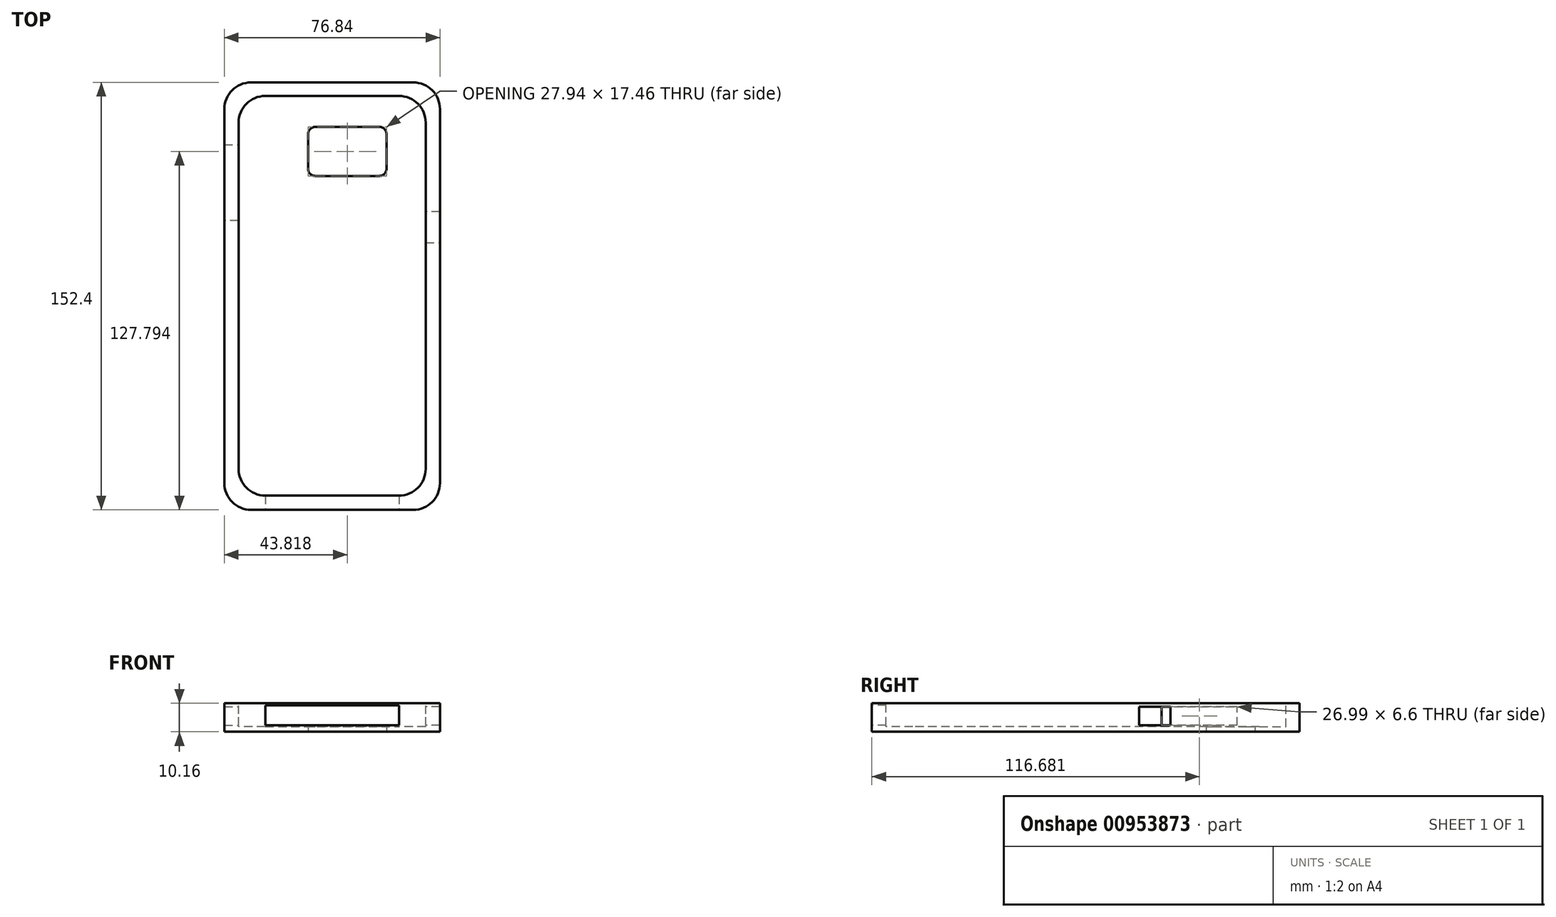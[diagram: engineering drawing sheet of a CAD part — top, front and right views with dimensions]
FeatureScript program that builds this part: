
annotation { "Feature Type Name" : "Feature", "Feature Type Description" : "" }
export const myFeature = defineFeature(function(context is Context, id is Id, definition is map)
    precondition{}
    {
        {
            var Q0;
            Q0=qCreatedBy(makeId("Top.planeOp"),FACE);
            var sketch = newSketch(context, id + "F0", { "sketchPlane" : qUnion([Q0])});
            skLineSegment(sketch, "E0.bottom", {"start": v(33.34, -71.12) * mm, "end": v(-33.34, -71.12) * mm});
            skLineSegment(sketch, "E0.top", {"start": v(33.34, 71.12) * mm, "end": v(-33.34, 71.12) * mm});
            skLineSegment(sketch, "E0.left", {"start": v(33.34, -71.12) * mm, "end": v(33.34, 71.12) * mm});
            skLineSegment(sketch, "E0.right", {"start": v(-33.34, -71.12) * mm, "end": v(-33.34, 71.12) * mm});
            skPoint(sketch, "E0.middle", {"position": v(0, 0) * mm});
            skPoint(sketch, "E1.endSnap0", {"position": v(0, -76.2) * mm});
            skLineSegment(sketch, "E2", {"start": v(38.42, -76.2) * mm, "end": v(38.42, 76.2) * mm});
            skLineSegment(sketch, "E3", {"start": v(38.42, 76.2) * mm, "end": v(-38.42, 76.2) * mm});
            skLineSegment(sketch, "E4", {"start": v(-38.42, 76.2) * mm, "end": v(-38.42, -76.2) * mm});
            skLineSegment(sketch, "E5", {"start": v(38.42, -76.2) * mm, "end": v(-38.42, -76.2) * mm});
            skLineSegment(sketch, "E6", {"start": v(-33.34, -71.12) * mm, "end": v(-33.34, -76.2) * mm});
            skSolve(sketch);
        }
        {
            var Q0;
            Q0=makeQuery(id+"F0.imprint","IMPRINT",FACE,{"disambiguationData":[TD([[makeQuery(id+"F0.imprint","IMPRINT",EDGE,{"derivedFrom":sQuery(id+"F0.wireOp",EDGE,"E0.bottom")}),1.0]])]});
            var Q1;
            Q1=makeQuery(id+"F0.imprint","IMPRINT",FACE,{"disambiguationData":[TD([[makeQuery(id+"F0.imprint","IMPRINT",EDGE,{"derivedFrom":sQuery(id+"F0.wireOp",EDGE,"E0.bottom")}),-1.0]])]});
            extrude(context, id + "F1", {"entities" : qUnion([Q0, Q1]), "depth" : 10.16 * mm, "offsetDistance" : 25.4 * mm});
        }
        {
            var Q0;
            Q0=makeQuery(id+"F1.opExtrude","CAP_FACE",FACE,{"disambiguationData":[OSD([sQuery(id+"F0.wireOp",EDGE,"E2"),sQuery(id+"F0.wireOp",EDGE,"E3"),sQuery(id+"F0.wireOp",EDGE,"E4"),sQuery(id+"F0.wireOp",EDGE,"E5")])],"isStart":false});
            var sketch = newSketch(context, id + "F2", { "sketchPlane" : qUnion([Q0])});
            skLineSegment(sketch, "E7", {"start": v(-38.42, -76.2) * mm, "end": v(-33.34, -76.2) * mm});
            skLineSegment(sketch, "E8", {"start": v(-33.34, -76.2) * mm, "end": v(-33.34, -71.12) * mm});
            skLineSegment(sketch, "E9", {"start": v(-33.34, -71.12) * mm, "end": v(33.34, -71.12) * mm});
            skLineSegment(sketch, "E10", {"start": v(33.34, -71.12) * mm, "end": v(33.34, 71.37) * mm});
            skLineSegment(sketch, "E11", {"start": v(33.34, 71.37) * mm, "end": v(-33.34, 71.37) * mm});
            skLineSegment(sketch, "E12", {"start": v(-33.34, 71.37) * mm, "end": v(-33.34, -71.12) * mm});
            skSolve(sketch);
        }
        {
            var Q0;
            Q0=makeQuery(id+"F2.imprint","IMPRINT",FACE,{"disambiguationData":[TD([[makeQuery(id+"F2.imprint","IMPRINT",EDGE,{"derivedFrom":sQuery(id+"F2.wireOp",EDGE,"E9")}),1.0]])]});
            extrude(context, id + "F3", {"entities" : qUnion([Q0]), "operationType" : NewBodyOperationType.REMOVE, "oppositeDirection" : true, "depth" : 8.38 * mm, "offsetDistance" : 25.4 * mm});
        }
        {
            var Q0;
            Q0=makeQuery(id+"F1.opExtrude","SWEPT_EDGE",EDGE,{"disambiguationData":[OSD([sQuery(id+"F0.wireOp",EDGE,"E3"),sQuery(id+"F0.wireOp",EDGE,"E4")])]});
            var Q1;
            Q1=makeQuery(id+"F1.opExtrude","SWEPT_EDGE",EDGE,{"disambiguationData":[OSD([sQuery(id+"F0.wireOp",EDGE,"E4"),sQuery(id+"F0.wireOp",EDGE,"E5")])]});
            var Q2;
            Q2=makeQuery(id+"F3.boolean.opBoolean","COPY",EDGE,{"derivedFrom":makeQuery(id+"F3.opExtrude","SWEPT_EDGE",EDGE,{"disambiguationData":[OSD([sQuery(id+"F2.wireOp",EDGE,"E11"),sQuery(id+"F2.wireOp",EDGE,"E12")])]})});
            var Q3;
            Q3=makeQuery(id+"F3.boolean.opBoolean","COPY",EDGE,{"derivedFrom":makeQuery(id+"F3.opExtrude","SWEPT_EDGE",EDGE,{"disambiguationData":[OSD([sQuery(id+"F2.wireOp",EDGE,"E9"),sQuery(id+"F2.wireOp",EDGE,"E12")])]})});
            var Q4;
            Q4=makeQuery(id+"F3.boolean.opBoolean","COPY",EDGE,{"derivedFrom":makeQuery(id+"F3.opExtrude","SWEPT_EDGE",EDGE,{"disambiguationData":[OSD([sQuery(id+"F2.wireOp",EDGE,"E9"),sQuery(id+"F2.wireOp",EDGE,"E10")])]})});
            var Q5;
            Q5=makeQuery(id+"F1.opExtrude","SWEPT_EDGE",EDGE,{"disambiguationData":[OSD([sQuery(id+"F0.wireOp",EDGE,"E2"),sQuery(id+"F0.wireOp",EDGE,"E5")])]});
            var Q6;
            Q6=makeQuery(id+"F1.opExtrude","SWEPT_EDGE",EDGE,{"disambiguationData":[OSD([sQuery(id+"F0.wireOp",EDGE,"E2"),sQuery(id+"F0.wireOp",EDGE,"E3")])]});
            var Q7;
            Q7=makeQuery(id+"F3.boolean.opBoolean","COPY",EDGE,{"derivedFrom":makeQuery(id+"F3.opExtrude","SWEPT_EDGE",EDGE,{"disambiguationData":[OSD([sQuery(id+"F2.wireOp",EDGE,"E10"),sQuery(id+"F2.wireOp",EDGE,"E11")])]})});
            fillet(context, id + "F4", {"entities" : qUnion([Q0, Q1, Q2, Q3, Q4, Q5, Q6, Q7]), "radius" : 9.52 * mm, "tangentPropagation" : true, "allowEdgeOverflow" : false});
        }
        {
            var Q0;
            Q0=makeQuery(id+"F1.opExtrude","CAP_FACE",FACE,{"disambiguationData":[OSD([sQuery(id+"F0.wireOp",EDGE,"E2"),sQuery(id+"F0.wireOp",EDGE,"E3"),sQuery(id+"F0.wireOp",EDGE,"E4"),sQuery(id+"F0.wireOp",EDGE,"E5")])],"isStart":false});
            var sketch = newSketch(context, id + "F5", { "sketchPlane" : qUnion([Q0])});
            skLineSegment(sketch, "E13", {"start": v(-38.42, 76.2) * mm, "end": v(-28.9, 76.2) * mm});
            skLineSegment(sketch, "E14", {"start": v(-38.42, 76.2) * mm, "end": v(-38.42, 53.98) * mm});
            skLineSegment(sketch, "E15", {"start": v(-38.42, 53.98) * mm, "end": v(-38.42, 26.99) * mm});
            skLineSegment(sketch, "E16", {"start": v(-28.9, 76.2) * mm, "end": v(38.42, 76.2) * mm});
            skLineSegment(sketch, "E17", {"start": v(38.42, 76.2) * mm, "end": v(38.42, 30.16) * mm});
            skLineSegment(sketch, "E18", {"start": v(38.42, 30.16) * mm, "end": v(38.42, 19.05) * mm});
            skLineSegment(sketch, "E19", {"start": v(38.42, 30.16) * mm, "end": v(33.34, 30.16) * mm});
            skLineSegment(sketch, "E20", {"start": v(33.34, 19.05) * mm, "end": v(38.42, 19.05) * mm});
            skLineSegment(sketch, "E21", {"start": v(33.34, 30.16) * mm, "end": v(33.34, 19.05) * mm});
            skLineSegment(sketch, "E22", {"start": v(-38.42, 53.98) * mm, "end": v(-33.34, 53.98) * mm});
            skLineSegment(sketch, "E23", {"start": v(-33.34, 53.98) * mm, "end": v(-33.34, 26.99) * mm});
            skLineSegment(sketch, "E24", {"start": v(-33.34, 26.99) * mm, "end": v(-38.42, 26.99) * mm});
            skLineSegment(sketch, "E25", {"start": v(23.81, -71.12) * mm, "end": v(-23.81, -71.12) * mm});
            skLineSegment(sketch, "E26", {"start": v(-23.81, -71.12) * mm, "end": v(-23.81, -76.2) * mm});
            skLineSegment(sketch, "E27", {"start": v(-23.81, -76.2) * mm, "end": v(23.81, -76.2) * mm});
            skLineSegment(sketch, "E28", {"start": v(23.81, -71.12) * mm, "end": v(23.81, -76.2) * mm});
            skSolve(sketch);
        }
        {
            var Q0;
            Q0=makeQuery(id+"F5.imprint","IMPRINT",FACE,{"disambiguationData":[TD([[makeQuery(id+"F5.imprint","IMPRINT",EDGE,{"derivedFrom":sQuery(id+"F5.wireOp",EDGE,"E25")}),-1.0]])]});
            var Q1;
            Q1=makeQuery(id+"F5.imprint","IMPRINT",FACE,{"disambiguationData":[TD([[makeQuery(id+"F5.imprint","IMPRINT",EDGE,{"derivedFrom":sQuery(id+"F5.wireOp",EDGE,"E18")}),1.0]])]});
            var Q2;
            Q2=makeQuery(id+"F5.imprint","IMPRINT",FACE,{"disambiguationData":[TD([[makeQuery(id+"F5.imprint","IMPRINT",EDGE,{"derivedFrom":sQuery(id+"F5.wireOp",EDGE,"E15")}),1.0]])]});
            extrude(context, id + "F6", {"entities" : qUnion([Q0, Q1, Q2]), "operationType" : NewBodyOperationType.REMOVE, "oppositeDirection" : true, "depth" : 7.87 * mm, "offsetDistance" : 25.4 * mm});
        }
        {
            var Q0;
            Q0=makeQuery(id+"F1.opExtrude","CAP_FACE",FACE,{"disambiguationData":[OSD([sQuery(id+"F0.wireOp",EDGE,"E2"),sQuery(id+"F0.wireOp",EDGE,"E3"),sQuery(id+"F0.wireOp",EDGE,"E4"),sQuery(id+"F0.wireOp",EDGE,"E5")])],"isStart":true});
            var sketch = newSketch(context, id + "F7", { "sketchPlane" : qUnion([Q0])});
            skLineSegment(sketch, "E29", {"start": v(28.9, -76.2) * mm, "end": v(38.42, -76.2) * mm});
            skLineSegment(sketch, "E30", {"start": v(38.42, -76.2) * mm, "end": v(38.42, -60.33) * mm});
            skLineSegment(sketch, "E31", {"start": v(38.42, -60.33) * mm, "end": v(19.37, -60.33) * mm});
            skLineSegment(sketch, "E32", {"start": v(19.37, -60.33) * mm, "end": v(19.37, -42.86) * mm});
            skLineSegment(sketch, "E33", {"start": v(19.37, -42.86) * mm, "end": v(-8.57, -42.86) * mm});
            skLineSegment(sketch, "E34", {"start": v(-8.57, -42.86) * mm, "end": v(-8.57, -60.33) * mm});
            skLineSegment(sketch, "E35", {"start": v(-8.57, -60.33) * mm, "end": v(19.37, -60.33) * mm});
            skSolve(sketch);
        }
        {
            var Q0;
            Q0=makeQuery(id+"F7.imprint","IMPRINT",FACE,{"disambiguationData":[TD([[makeQuery(id+"F7.imprint","IMPRINT",EDGE,{"derivedFrom":sQuery(id+"F7.wireOp",EDGE,"E32")}),1.0]])]});
            extrude(context, id + "F8", {"entities" : qUnion([Q0]), "operationType" : NewBodyOperationType.REMOVE, "oppositeDirection" : true, "depth" : 2.3 * mm, "offsetDistance" : 25.4 * mm});
        }
        {
            var Q0;
            Q0=makeQuery(id+"F8.boolean.opBoolean","COPY",EDGE,{"derivedFrom":makeQuery(id+"F8.opExtrude","SWEPT_EDGE",EDGE,{"disambiguationData":[OSD([sQuery(id+"F7.wireOp",EDGE,"E32"),sQuery(id+"F7.wireOp",EDGE,"E35")])]})});
            var Q1;
            Q1=makeQuery(id+"F8.boolean.opBoolean","COPY",EDGE,{"derivedFrom":makeQuery(id+"F8.opExtrude","SWEPT_EDGE",EDGE,{"disambiguationData":[OSD([sQuery(id+"F7.wireOp",EDGE,"E34"),sQuery(id+"F7.wireOp",EDGE,"E35")])]})});
            var Q2;
            Q2=makeQuery(id+"F8.boolean.opBoolean","COPY",EDGE,{"derivedFrom":makeQuery(id+"F8.opExtrude","SWEPT_EDGE",EDGE,{"disambiguationData":[OSD([sQuery(id+"F7.wireOp",EDGE,"E33"),sQuery(id+"F7.wireOp",EDGE,"E34")])]})});
            var Q3;
            Q3=makeQuery(id+"F8.boolean.opBoolean","COPY",EDGE,{"derivedFrom":makeQuery(id+"F8.opExtrude","SWEPT_EDGE",EDGE,{"disambiguationData":[OSD([sQuery(id+"F7.wireOp",EDGE,"E32"),sQuery(id+"F7.wireOp",EDGE,"E33")])]})});
            fillet(context, id + "F9", {"entities" : qUnion([Q0, Q1, Q2, Q3]), "radius" : 2.54 * mm, "tangentPropagation" : true, "allowEdgeOverflow" : false});
        }
        {
            var Q0;
            {var subQ0=sQuery(id+"F0.wireOp",EDGE,"E5");var subQ1=sQuery(id+"F0.wireOp",EDGE,"E4");Q0=makeQuery(id+"F6.boolean.opBoolean","SPLIT",FACE,{"disambiguationData":[TD([makeQuery(id+"F6.opExtrude","SWEPT_FACE",FACE,{"disambiguationData":[OSD([sQuery(id+"F5.wireOp",EDGE,"E24")])]})])],"derivedFrom":makeQuery(id+"F1.opExtrude","CAP_FACE",FACE,{"disambiguationData":[OSD([sQuery(id+"F0.wireOp",EDGE,"E2"),sQuery(id+"F0.wireOp",EDGE,"E3"),subQ1,subQ0])],"isStart":false})});}
            var sketch = newSketch(context, id + "F10", { "sketchPlane" : qUnion([Q0])});
            skLineSegment(sketch, "E36", {"start": v(-38.42, 26.99) * mm, "end": v(-38.42, 53.98) * mm});
            skLineSegment(sketch, "E37", {"start": v(-38.42, 53.98) * mm, "end": v(-33.34, 53.98) * mm});
            skLineSegment(sketch, "E38", {"start": v(-33.34, 53.98) * mm, "end": v(-33.34, 26.99) * mm});
            skLineSegment(sketch, "E39", {"start": v(-33.34, 26.99) * mm, "end": v(-38.42, 26.99) * mm});
            skSolve(sketch);
        }
        {
            var Q0;
            Q0=makeQuery(id+"F10.imprint","IMPRINT",FACE,{"disambiguationData":[TD([[makeQuery(id+"F10.imprint","IMPRINT",EDGE,{"derivedFrom":sQuery(id+"F10.wireOp",EDGE,"E36")}),-1.0]])]});
            extrude(context, id + "F11", {"entities" : qUnion([Q0]), "operationType" : NewBodyOperationType.ADD, "oppositeDirection" : true, "depth" : 1.27 * mm, "offsetDistance" : 25.4 * mm});
        }
        {
            var Q0;
            {var subQ1=sQuery(id+"F0.wireOp",EDGE,"E5");var subQ2=sQuery(id+"F0.wireOp",EDGE,"E2");Q0=makeQuery(id+"F6.boolean.opBoolean","SPLIT",FACE,{"disambiguationData":[TD([makeQuery(id+"F6.opExtrude","SWEPT_FACE",FACE,{"disambiguationData":[OSD([sQuery(id+"F5.wireOp",EDGE,"E20")])]})])],"derivedFrom":makeQuery(id+"F1.opExtrude","CAP_FACE",FACE,{"disambiguationData":[OSD([subQ2,sQuery(id+"F0.wireOp",EDGE,"E3"),sQuery(id+"F0.wireOp",EDGE,"E4"),subQ1])],"isStart":false})});}
            var sketch = newSketch(context, id + "F12", { "sketchPlane" : qUnion([Q0])});
            skLineSegment(sketch, "E40", {"start": v(33.34, 19.05) * mm, "end": v(33.34, 30.16) * mm});
            skLineSegment(sketch, "E41", {"start": v(33.34, 19.05) * mm, "end": v(38.42, 19.05) * mm});
            skLineSegment(sketch, "E42", {"start": v(38.42, 19.05) * mm, "end": v(38.42, 30.16) * mm});
            skLineSegment(sketch, "E43", {"start": v(38.42, 30.16) * mm, "end": v(33.34, 30.16) * mm});
            skSolve(sketch);
        }
        {
            var Q0;
            Q0=makeQuery(id+"F12.imprint","IMPRINT",FACE,{"disambiguationData":[TD([[makeQuery(id+"F12.imprint","IMPRINT",EDGE,{"derivedFrom":sQuery(id+"F12.wireOp",EDGE,"E40")}),-1.0]])]});
            extrude(context, id + "F13", {"entities" : qUnion([Q0]), "operationType" : NewBodyOperationType.ADD, "oppositeDirection" : true, "depth" : 1.27 * mm, "offsetDistance" : 25.4 * mm});
        }
        {
            var Q0;
            {var subQ2=sQuery(id+"F0.wireOp",EDGE,"E3");var subQ3=sQuery(id+"F0.wireOp",EDGE,"E2");var subQ6=sQuery(id+"F0.wireOp",EDGE,"E4");var subQ10=sQuery(id+"F0.wireOp",EDGE,"E5");var subQ11=makeQuery(id+"F1.opExtrude","CAP_FACE",FACE,{"disambiguationData":[OSD([subQ3,subQ2,subQ6,subQ10])],"isStart":false});Q0=makeQuery(id+"F13.boolean.opBoolean","MERGE",FACE,{"derivedFrom":[makeQuery(id+"F6.boolean.opBoolean","SPLIT",FACE,{"disambiguationData":[TD([makeQuery(id+"F6.opExtrude","SWEPT_FACE",FACE,{"disambiguationData":[OSD([sQuery(id+"F5.wireOp",EDGE,"E20")])]})])],"derivedFrom":subQ11}),makeQuery(id+"F11.boolean.opBoolean","MERGE",FACE,{"derivedFrom":[makeQuery(id+"F6.boolean.opBoolean","SPLIT",FACE,{"disambiguationData":[TD([makeQuery(id+"F6.opExtrude","SWEPT_FACE",FACE,{"disambiguationData":[OSD([sQuery(id+"F5.wireOp",EDGE,"E24")])]})])],"derivedFrom":subQ11}),makeQuery(id+"F6.boolean.opBoolean","SPLIT",FACE,{"disambiguationData":[TD([makeQuery(id+"F1.opExtrude","SWEPT_FACE",FACE,{"disambiguationData":[OSD([subQ2])]})])],"derivedFrom":subQ11}),makeQuery(id+"F11.opExtrude","CAP_FACE",FACE,{"disambiguationData":[OSD([sQuery(id+"F10.wireOp",EDGE,"E36"),sQuery(id+"F10.wireOp",EDGE,"E37"),sQuery(id+"F10.wireOp",EDGE,"E38"),sQuery(id+"F10.wireOp",EDGE,"E39")])],"isStart":true})]}),makeQuery(id+"F13.opExtrude","CAP_FACE",FACE,{"disambiguationData":[OSD([sQuery(id+"F12.wireOp",EDGE,"E40"),sQuery(id+"F12.wireOp",EDGE,"E41"),sQuery(id+"F12.wireOp",EDGE,"E42"),sQuery(id+"F12.wireOp",EDGE,"E43")])],"isStart":true})]});}
            var sketch = newSketch(context, id + "F14", { "sketchPlane" : qUnion([Q0])});
            skLineSegment(sketch, "E44", {"start": v(-23.81, -71.12) * mm, "end": v(23.81, -71.12) * mm});
            skLineSegment(sketch, "E45", {"start": v(23.81, -71.12) * mm, "end": v(23.81, -76.2) * mm});
            skLineSegment(sketch, "E46", {"start": v(23.81, -76.2) * mm, "end": v(-23.81, -76.2) * mm});
            skLineSegment(sketch, "E47", {"start": v(-23.81, -76.2) * mm, "end": v(-23.81, -71.12) * mm});
            skSolve(sketch);
        }
        {
            var Q0;
            Q0=makeQuery(id+"F14.imprint","IMPRINT",FACE,{"disambiguationData":[TD([[makeQuery(id+"F14.imprint","IMPRINT",EDGE,{"derivedFrom":sQuery(id+"F14.wireOp",EDGE,"E44")}),-1.0]])]});
            extrude(context, id + "F15", {"entities" : qUnion([Q0]), "operationType" : NewBodyOperationType.ADD, "oppositeDirection" : true, "depth" : 0.76 * mm, "offsetDistance" : 25.4 * mm});
        }
    });
